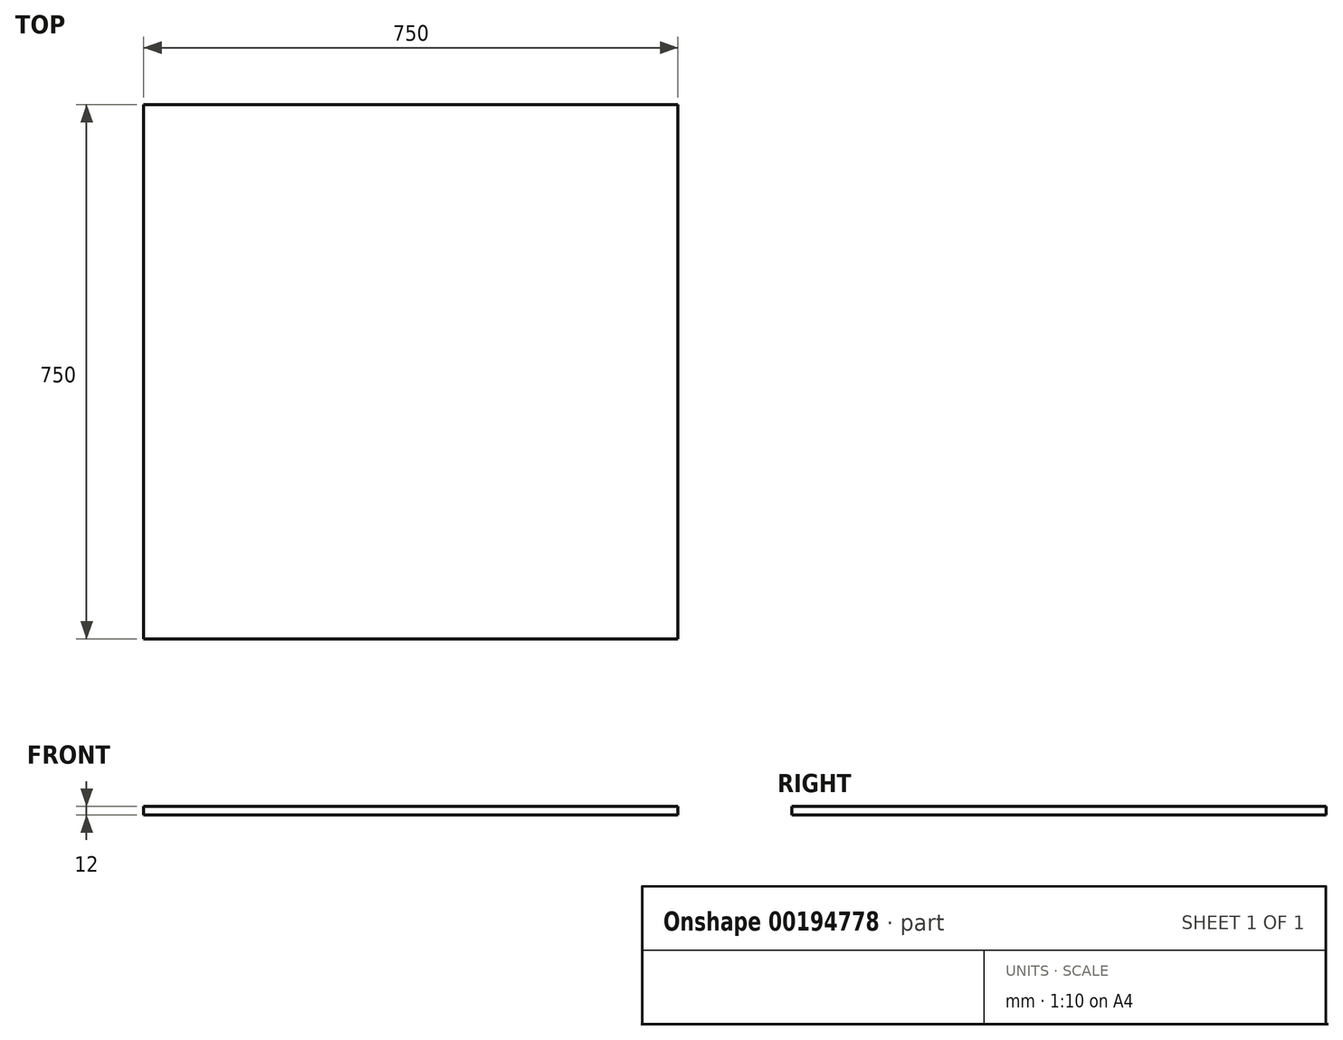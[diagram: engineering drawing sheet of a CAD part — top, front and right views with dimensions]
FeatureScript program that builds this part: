
annotation { "Feature Type Name" : "Feature", "Feature Type Description" : "" }
export const myFeature = defineFeature(function(context is Context, id is Id, definition is map)
    precondition{}
    {
        {
            var Q0;
            Q0=qCreatedBy(makeId("Top.planeOp"),FACE);
            var sketch = newSketch(context, id + "F0", { "sketchPlane" : qUnion([Q0])});
            skLineSegment(sketch, "E0.bottom", {"start": v(-375, 375) * mm, "end": v(375, 375) * mm});
            skLineSegment(sketch, "E0.top", {"start": v(-375, -375) * mm, "end": v(375, -375) * mm});
            skLineSegment(sketch, "E0.left", {"start": v(-375, 375) * mm, "end": v(-375, -375) * mm});
            skLineSegment(sketch, "E0.right", {"start": v(375, 375) * mm, "end": v(375, -375) * mm});
            skPoint(sketch, "E0.middle", {"position": v(0, 0) * mm});
            skSolve(sketch);
        }
        {
            var Q0;
            Q0=qSketchRegion(id+"F0",true);
            extrude(context, id + "F1", {"entities" : qUnion([Q0]), "depth" : 12 * mm});
        }
        {
            var Q0;
            Q0=makeQuery(id+"F1.opExtrude","CAP_FACE",FACE,{"disambiguationData":[OSD([sQuery(id+"F0.wireOp",EDGE,"E0.bottom"),sQuery(id+"F0.wireOp",EDGE,"E0.top"),sQuery(id+"F0.wireOp",EDGE,"E0.left"),sQuery(id+"F0.wireOp",EDGE,"E0.right")])],"isStart":false});
            var sketch = newSketch(context, id + "F2", { "sketchPlane" : qUnion([Q0])});
            skLineSegment(sketch, "E1.bottom", {"start": v(-90, 90) * mm, "end": v(90, 90) * mm});
            skLineSegment(sketch, "E1.top", {"start": v(-90, -90) * mm, "end": v(90, -90) * mm});
            skLineSegment(sketch, "E1.left", {"start": v(-90, 90) * mm, "end": v(-90, -90) * mm});
            skLineSegment(sketch, "E1.right", {"start": v(90, 90) * mm, "end": v(90, -90) * mm});
            skPoint(sketch, "E1.middle", {"position": v(0, 0) * mm});
            skSolve(sketch);
        }
        {
            var Q0;
            Q0=makeQuery(id+"F2.imprint","IMPRINT",FACE,{"disambiguationData":[TD([[makeQuery(id+"F2.imprint","IMPRINT",EDGE,{"derivedFrom":sQuery(id+"F2.wireOp",EDGE,"E1.bottom")}),-1.0]])]});
            extrude(context, id + "F3", {"entities" : qUnion([Q0]), "operationType" : NewBodyOperationType.REMOVE, "oppositeDirection" : true, "depth" : 25 * mm});
        }
        {
            var Q0;
            Q0=makeQuery(id+"F1.opExtrude","CAP_FACE",FACE,{"disambiguationData":[OSD([sQuery(id+"F0.wireOp",EDGE,"E0.bottom"),sQuery(id+"F0.wireOp",EDGE,"E0.top"),sQuery(id+"F0.wireOp",EDGE,"E0.left"),sQuery(id+"F0.wireOp",EDGE,"E0.right")])],"isStart":false});
            var sketch = newSketch(context, id + "F4", { "sketchPlane" : qUnion([Q0])});
            skLineSegment(sketch, "E2.bottom", {"start": v(90, 90) * mm, "end": v(-90, 90) * mm});
            skLineSegment(sketch, "E2.top", {"start": v(90, -90) * mm, "end": v(-90, -90) * mm});
            skLineSegment(sketch, "E2.left", {"start": v(90, 90) * mm, "end": v(90, -90) * mm});
            skLineSegment(sketch, "E2.right", {"start": v(-90, 90) * mm, "end": v(-90, -90) * mm});
            skSolve(sketch);
        }
        {
            var Q0;
            Q0=qSketchRegion(id+"F4",true);
            extrude(context, id + "F5", {"entities" : qUnion([Q0]), "operationType" : NewBodyOperationType.ADD, "oppositeDirection" : true, "depth" : 12 * mm, "hasSecondDirection" : true, "secondDirectionOppositeDirection" : true, "secondDirectionDepth" : 0.01 * mm});
        }
    });
